# Revit family: AQUA+VS
name_source: partatom
category: Attrezzature speciali
revit_build: Autodesk Revit 2017 (Build: 20160225_1515(x64)
units: mm (PartAtom-declared; Revit-internal decimal feet)

## family parameters
Basato su piano di lavoro = No
Condiviso = No
Punto di calcolo locali = No
Quota connettore circolare = Usa diametro
Sempre verticale = Sì
Taglio con vuoti quando caricato = No
Tipo di parte = Normale

## types (1)
- AQUA+VS
    Electrical supply = 230 V
    Height = 461 mm  [stored 1.51247 ft]
    Installed Load = 0.2 kW
    Length = 561 mm
    Max supply pressure = 600.0 kPa
    Minimum supply flow = 0.1 L/s
    Minimum supply pressure = 100.0 kPa
    Tank drain = 6 mm  [stored 0.019685 ft]
    Total absorption = 2 A
    Water inlet = 1"
    Weight = 20.00 kg
    Width = 148 mm  [stored 0.485564 ft]

note: [stored X ft] marks values corroborated as IEEE doubles in the binary element streams (Revit-internal decimal feet)

## geometry (parser evidence)
native form markers: Blend x2
no freeform markers — native parametric forms only
